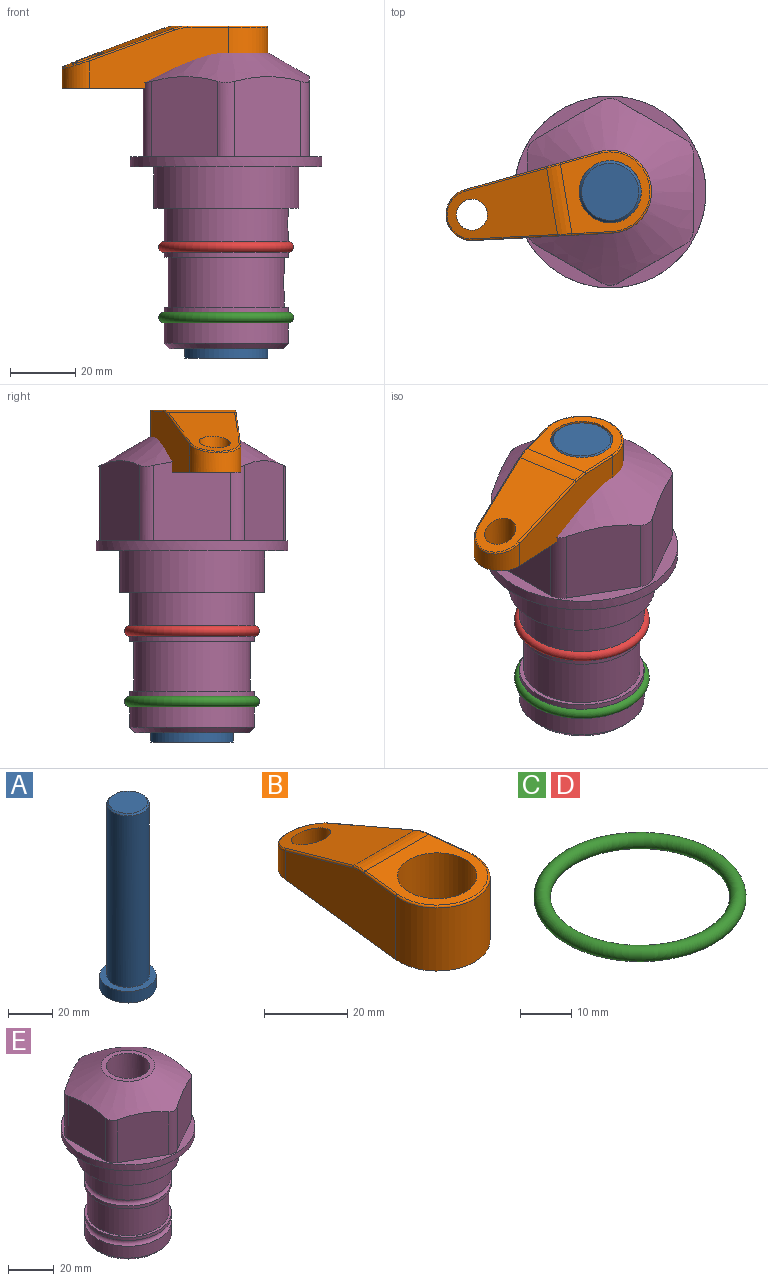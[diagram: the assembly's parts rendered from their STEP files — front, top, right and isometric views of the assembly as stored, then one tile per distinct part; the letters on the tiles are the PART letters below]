
ASSEMBLY  parts=5 mates=3
PART A: 6 faces, bbox 25.4x25.4x101.6 mm
  f0: plane 17.46x17.46mm, normal (0,0,1), area 239.5mm2, adj f5
  f1: plane 25.4x25.4mm, normal (0,0,-1), area 506.7mm2, adj f2
  f2: cylinder r=12.7mm len=25.4mm, axis (0,0,1), area 506.7mm2, adj f1,f3
  f3: plane 25.4x25.4mm, normal (0,0,1), area 221.7mm2, adj f2,f4
  f4: cylinder r=9.53mm len=94.46mm, axis (0,0,1), area 5653mm2, adj f3,f5
  f5: cone r=8.73mm half-angle=45deg, axis (0,0,-1), area 64.4mm2, adj f0,f4
PART B: 44 faces, bbox 27.5x64.5x19.1 mm
  f0: plane 2.3x0.95mm, normal (0,0,-1), area 1mm2, adj f25,f30,f34
  f1: plane 63.5x25.4mm, normal (0,0,-1), area 561.7mm2, adj f2,f3,f4,f5,f6,f7,f19,f20
  f2: cylinder r=12.7mm len=25.4mm, axis (0,0,-1), area 792.2mm2, adj f1,f3,f5,f13
  f3: plane 42.33x18.54mm, normal (0.99,0.11,0), area 647mm2, adj f1,f2,f4,f11,f12,f14
  f4: cylinder r=7.94mm len=15.78mm, axis (0,0,-1), area 158.6mm2, adj f1,f3,f5,f16
  f5: plane 42.33x18.54mm, normal (-0.99,0.11,0), area 647mm2, adj f1,f2,f4,f15,f17,f18
  f6: cylinder r=9.53mm len=19.05mm, axis (0,0,-1), area 1140.1mm2, adj f1,f8
  f7: cylinder r=4.76mm len=10.98mm, axis (0,0,-1), area 276.1mm2, adj f1,f9
  f8: plane 25.83x24.38mm, normal (0,0,1), area 262.2mm2, adj f6,f10,f11,f13,f15
  f9: plane 32.49x20.55mm, normal (0,0.34,0.94), area 489.9mm2, adj f7,f10,f14,f16,f18
  f10: cylinder r=12.7mm len=21.49mm, axis (-1,0,0), area 93.2mm2, adj f8,f9,f12,f17
  f11: cylinder r=0.51mm len=12.34mm, axis (0.11,-0.99,0), area 9.9mm2, adj f3,f8,f12,f13
  f12: bspline ~7.62x1.64mm, area 3.5mm2, adj f3,f10,f11,f14
  f13: torus R=12.19mm, axis (0,0,1), area 33.6mm2, adj f2,f8,f11,f15
  f14: cylinder r=0.51mm len=26.01mm, axis (0.1,-0.93,0.34), area 21.6mm2, adj f3,f9,f12,f16
  f15: cylinder r=0.51mm len=12.34mm, axis (0.11,0.99,0), area 9.9mm2, adj f5,f8,f13,f17
  f16: bspline ~15.78x7.05mm, area 15.7mm2, adj f4,f9,f14,f18
  f17: bspline ~7.62x1.64mm, area 3.5mm2, adj f5,f10,f15,f18
  f18: cylinder r=0.51mm len=26.01mm, axis (0.1,0.93,-0.34), area 21.6mm2, adj f5,f9,f16,f17
  f19: plane 21.6x14.29mm, normal (-0.99,-0.11,0), area 242.6mm2, adj f1,f26,f28,f34,f36,f38
  f20: plane 21.6x14.29mm, normal (0.99,-0.11,0), area 242.6mm2, adj f1,f27,f29,f37,f39,f41
  f21: cylinder r=12.7mm len=14.29mm, axis (0,0,-1), area 173.2mm2, adj f1,f26,f27,f30,f31,f33
  f22: cylinder r=7.94mm len=7.63mm, axis (0,0,-1), area 53.8mm2, adj f1,f28,f29,f42
  f23: plane 2.3x0.95mm, normal (0,0,-1), area 1mm2, adj f25,f33,f37
  f24: plane 17.94x12.32mm, normal (0,-0.34,-0.94), area 191.2mm2, adj f25,f38,f41,f42
  f25: cylinder r=9.53mm len=12.93mm, axis (-1,0,0), area 37.5mm2, adj f0,f23,f24,f31,f36,f39
  f26: cylinder r=1.59mm len=14.29mm, axis (0,0,-1), area 49mm2, adj f1,f19,f21,f32
  f27: cylinder r=1.59mm len=14.29mm, axis (0,0,-1), area 49mm2, adj f1,f20,f21,f35
  f28: cylinder r=1.59mm len=7.28mm, axis (0,0,-1), area 22.1mm2, adj f1,f19,f22,f40
  f29: cylinder r=1.59mm len=7.28mm, axis (0,0,-1), area 22.1mm2, adj f1,f20,f22,f43
  f30: torus R=14.29mm, axis (0,0,1), area 5.8mm2, adj f0,f21,f31,f32
  f31: bspline ~11.06x2.73mm, area 20.8mm2, adj f21,f25,f30,f33
  f32: sphere r=1.59mm, area 5.4mm2, adj f26,f30,f34
  f33: torus R=14.29mm, axis (0,0,1), area 5.8mm2, adj f21,f23,f31,f35
  f34: cylinder r=1.59mm len=1.68mm, axis (-0.11,0.99,0), area 2.4mm2, adj f0,f19,f32,f36
  f35: sphere r=1.59mm, area 5.4mm2, adj f27,f33,f37
  f36: bspline ~5.82x2.33mm, area 7.7mm2, adj f19,f25,f34,f38
  f37: cylinder r=1.59mm len=1.68mm, axis (0.11,0.99,0), area 2.4mm2, adj f20,f23,f35,f39
  f38: cylinder r=1.59mm len=18.33mm, axis (0.1,-0.93,0.34), area 46.7mm2, adj f19,f24,f36,f40
  f39: bspline ~5.82x2.33mm, area 7.7mm2, adj f20,f25,f37,f41
  f40: sphere r=1.59mm, area 3.6mm2, adj f28,f38,f42
  f41: cylinder r=1.59mm len=18.33mm, axis (0.1,0.93,-0.34), area 46.7mm2, adj f20,f24,f39,f43
  f42: bspline ~8.31x1.84mm, area 15.3mm2, adj f22,f24,f40,f43
  f43: sphere r=1.59mm, area 3.6mm2, adj f29,f41,f42
PART C: 1 faces, bbox 44.7x44.7x3.2 mm
  f0: torus R=19.05mm, axis (0,0,1), area 1193.9mm2
PART D: same geometry as C
PART E: 36 faces, bbox 58.7x58.7x91.2 mm
  f0: cylinder r=17.78mm len=35.56mm, axis (0,0,1), area 1670.8mm2, adj f23,f24,f31
  f1: cylinder r=19.05mm len=38.1mm, axis (0,0,1), area 1191.9mm2, adj f26,f27,f30
  f2: plane 58.66x58.66mm, normal (0,0,-1), area 1150.6mm2, adj f3,f28
  f3: cylinder r=29.33mm len=58.66mm, axis (0,0,-1), area 585.1mm2, adj f2,f4
  f4: plane 58.66x58.66mm, normal (0,0,1), area 475.9mm2, adj f3,f5,f6,f7,f8,f9,f10,f11
  f5: plane 24.5x20.32mm, normal (-0.5,0.87,0), area 562.8mm2, adj f4,f15,f16,f17
  f6: plane 24.5x20.32mm, normal (0.5,0.87,0), area 562.8mm2, adj f4,f14,f15,f17
  f7: plane 24.5x23.48mm, normal (1,0,0), area 562.8mm2, adj f4,f13,f14,f17
  f8: plane 24.5x20.32mm, normal (0.5,-0.87,0), area 562.8mm2, adj f4,f12,f13,f17
  f9: plane 24.5x20.32mm, normal (-0.5,-0.87,0), area 562.8mm2, adj f4,f11,f12,f17
  f10: plane 24.5x23.48mm, normal (-1,0,0), area 562.8mm2, adj f4,f11,f16,f17
  f11: cylinder r=5.08mm len=23.01mm, axis (0,0,-1), area 121.2mm2, adj f4,f9,f10,f17
  f12: cylinder r=5.08mm len=23.01mm, axis (0,0,-1), area 121.2mm2, adj f4,f8,f9,f17
  f13: cylinder r=5.08mm len=23.01mm, axis (0,0,-1), area 121.2mm2, adj f4,f7,f8,f17
  f14: cylinder r=5.08mm len=23.01mm, axis (0,0,-1), area 121.2mm2, adj f4,f6,f7,f17
  f15: cylinder r=5.08mm len=23.01mm, axis (0,0,-1), area 121.2mm2, adj f4,f5,f6,f17
  f16: cylinder r=5.08mm len=23.01mm, axis (0,0,-1), area 121.2mm2, adj f4,f5,f10,f17
  f17: cone r=11.73mm half-angle=60deg, axis (0,0,-1), area 2071.8mm2, adj f5,f6,f7,f8,f9,f10,f11,f12
  f18: plane 23.46x23.46mm, normal (0,0,1), area 147.4mm2, adj f17,f35
  f19: plane 34.93x34.93mm, normal (0,0,-1), area 958mm2, adj f29
  f20: cylinder r=19.05mm len=38.1mm, axis (0,0,1), area 760.1mm2, adj f21,f29
  f21: torus R=19.05mm, axis (0,0,1), area 565.3mm2, adj f20,f22
  f22: cylinder r=19.05mm len=38.1mm, axis (0,0,1), area 190mm2, adj f21,f23
  f23: plane 38.1x38.1mm, normal (0,0,1), area 146.9mm2, adj f0,f22
  f24: plane 38.1x38.1mm, normal (0,0,-1), area 146.9mm2, adj f0,f25
  f25: cylinder r=19.05mm len=38.1mm, axis (0,0,1), area 190mm2, adj f24,f26
  f26: torus R=19.05mm, axis (0,0,1), area 565.3mm2, adj f1,f25
  f27: plane 44.45x44.45mm, normal (0,0,-1), area 411.7mm2, adj f1,f28
  f28: cylinder r=22.23mm len=44.45mm, axis (0,0,1), area 1773.5mm2, adj f2,f27
  f29: cone r=19.05mm half-angle=45deg, axis (0,0,1), area 257.5mm2, adj f19,f20
  f30: cylinder r=3.17mm len=6.75mm, axis (-1,0,0), area 128mm2, adj f1,f33
  f31: cylinder r=3.17mm len=6.35mm, axis (-1,0,0), area 102.5mm2, adj f0,f33
  f32: plane 25.4x25.4mm, normal (0,0,1), area 506.7mm2, adj f33
  f33: cylinder r=12.7mm len=66.42mm, axis (0,0,-1), area 5236.2mm2, adj f30,f31,f32,f34
  f34: cone r=9.53mm half-angle=30deg, axis (0,0,-1), area 443.4mm2, adj f33,f35
  f35: cylinder r=9.53mm len=19.05mm, axis (0,0,-1), area 849mm2, adj f18,f34
PLACE A rot(axis=(0,0,-1),170.6deg) t=(0,0,-30.54)mm
PLACE B rot(axis=(0,0,1),99.4deg) t=(0,0,24.07)mm
PLACE C t=(0,0,-21.59)mm
PLACE D at identity
PLACE E at identity fixed
MATE fastened C.f0 <-> E.f0  axis (0,0,1) through (0,0,-46.1)mm
MATE cylindrical A.f2 <-> E.f0  axis (0,0,1) through (0,0,-4.9)mm
MATE fastened B.f2 <-> A.f2  axis (0,0,1) through (0,0,43.12)mm
